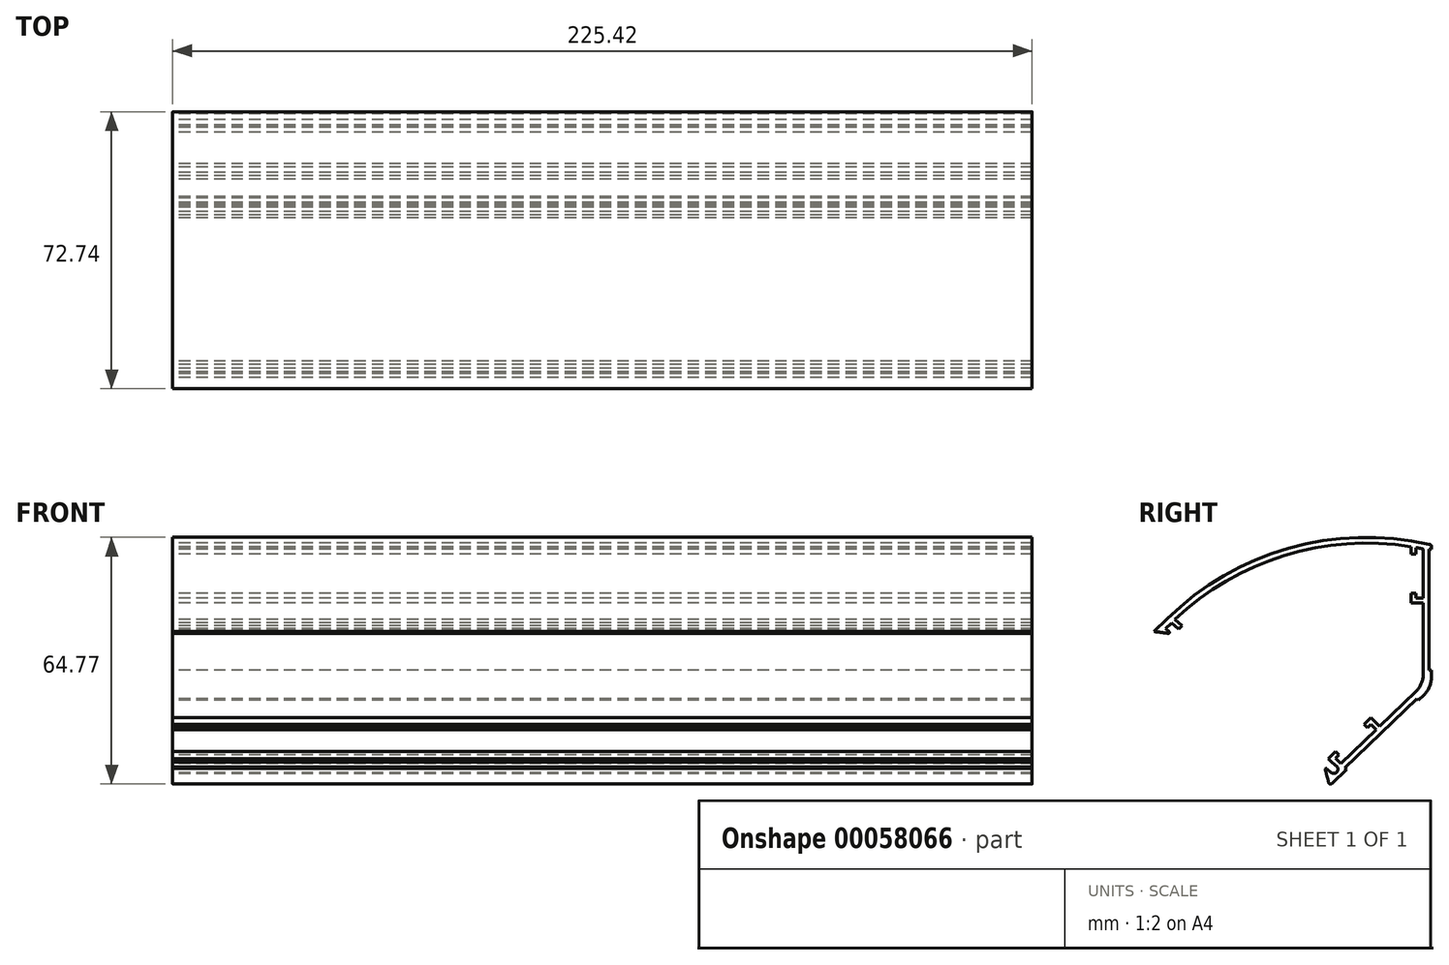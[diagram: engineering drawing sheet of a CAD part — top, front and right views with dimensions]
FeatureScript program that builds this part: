
annotation { "Feature Type Name" : "Feature", "Feature Type Description" : "" }
export const myFeature = defineFeature(function(context is Context, id is Id, definition is map)
    precondition{}
    {
        {
            var Q0;
            Q0=qCreatedBy(makeId("Right.planeOp"),FACE);
            var sketch = newSketch(context, id + "F0", { "sketchPlane" : qUnion([Q0])});
            skLineSegment(sketch, "E0", {"start": v(-26.31, -25.4) * mm, "end": v(0, 0) * mm});
            skLineSegment(sketch, "E1", {"start": v(0, 0) * mm, "end": v(0, 37.34) * mm});
            skArc(sketch, "E2", {"start": v(0, 37.34) * mm, "mid": v(-36.86, 36.32) * mm, "end": v(-68.74, 17.77) * mm});
            skLineSegment(sketch, "E3", {"start": v(-68.74, 17.77) * mm, "end": v(-72.14, 14.43) * mm});
            skLineSegment(sketch, "E4", {"start": v(-26.31, -25.4) * mm, "end": v(-72.14, 14.43) * mm});
            skLineSegment(sketch, "E5", {"start": v(-68.74, 17.77) * mm, "end": v(-26.31, -25.4) * mm, "construction": true});
            skSolve(sketch);
        }
        {
            var Q0;
            Q0=qSketchRegion(id+"F0",true);
            extrude(context, id + "F1", {"entities" : qUnion([Q0]), "endBound" : BoundingType.SYMMETRIC, "depth" : 225.42 * mm});
        }
        {
            var Q0;
            Q0=makeQuery(id+"F1.opExtrude","SWEPT_FACE",FACE,{"disambiguationData":[OSD([sQuery(id+"F0.wireOp",EDGE,"E4")])]});
            var Q1;
            Q1=makeQuery(id+"F1.opExtrude","CAP_FACE",FACE,{"disambiguationData":[OSD([sQuery(id+"F0.wireOp",EDGE,"E0"),sQuery(id+"F0.wireOp",EDGE,"E1"),sQuery(id+"F0.wireOp",EDGE,"E2"),sQuery(id+"F0.wireOp",EDGE,"E3"),sQuery(id+"F0.wireOp",EDGE,"E4")])],"isStart":true});
            var Q2;
            Q2=makeQuery(id+"F1.opExtrude","CAP_FACE",FACE,{"disambiguationData":[OSD([sQuery(id+"F0.wireOp",EDGE,"E0"),sQuery(id+"F0.wireOp",EDGE,"E1"),sQuery(id+"F0.wireOp",EDGE,"E2"),sQuery(id+"F0.wireOp",EDGE,"E3"),sQuery(id+"F0.wireOp",EDGE,"E4")])],"isStart":false});
            shell(context, id + "F2", {"entities" : qUnion([Q0, Q1, Q2]), "thickness" : 1.52 * mm});
        }
        {
            var Q0;
            Q0=makeQuery(id+"F1.opExtrude","CAP_FACE",FACE,{"disambiguationData":[OSD([sQuery(id+"F0.wireOp",EDGE,"E0"),sQuery(id+"F0.wireOp",EDGE,"E1"),sQuery(id+"F0.wireOp",EDGE,"E2"),sQuery(id+"F0.wireOp",EDGE,"E3"),sQuery(id+"F0.wireOp",EDGE,"E4")])],"isStart":true});
            var sketch = newSketch(context, id + "F3", { "sketchPlane" : qUnion([Q0])});
            skLineSegment(sketch, "E6", {"start": v(72.14, 14.43) * mm, "end": v(26.31, -25.4) * mm, "construction": true});
            skSolve(sketch);
        }
        {
            var Q0;
            {var subQ6=sQuery(id+"F0.wireOp",EDGE,"E0");var subQ7=makeQuery(id+"F1.opExtrude","CAP_EDGE",EDGE,{"disambiguationData":[OSD([subQ6])],"isStart":true});Q0=makeQuery(id+"F3.imprint","IMPRINT",FACE,{"disambiguationData":[TD([[makeQuery(id+"F3.imprint","IMPRINT",EDGE,{"derivedFrom":subQ7}),-1.0]])]});}
            var sketch = newSketch(context, id + "F4", { "sketchPlane" : qUnion([Q0])});
            skLineSegment(sketch, "E7", {"start": v(70.98, 13.42) * mm, "end": v(69.17, 15.2) * mm});
            skLineSegment(sketch, "E8", {"start": v(69.17, 15.2) * mm, "end": v(67.25, 13.54) * mm});
            skLineSegment(sketch, "E9", {"start": v(67.25, 13.54) * mm, "end": v(69.07, 11.76) * mm});
            skLineSegment(sketch, "E10", {"start": v(69.07, 11.76) * mm, "end": v(70.98, 13.42) * mm});
            skSolve(sketch);
        }
        {
            var Q0;
            Q0=qSketchRegion(id+"F4",true);
            var Q1;
            Q1=makeQuery(id+"F1.opExtrude","CAP_FACE",FACE,{"disambiguationData":[OSD([sQuery(id+"F0.wireOp",EDGE,"E0"),sQuery(id+"F0.wireOp",EDGE,"E1"),sQuery(id+"F0.wireOp",EDGE,"E2"),sQuery(id+"F0.wireOp",EDGE,"E3"),sQuery(id+"F0.wireOp",EDGE,"E4")])],"isStart":false});
            extrude(context, id + "F5", {"entities" : qUnion([Q0]), "operationType" : NewBodyOperationType.ADD, "endBound" : BoundingType.UP_TO_SURFACE, "oppositeDirection" : true, "endBoundEntityFace" : qUnion([Q1]), "depth" : 25.4 * mm});
        }
        {
            var Q0;
            {var subQ6=sQuery(id+"F0.wireOp",EDGE,"E0");var subQ7=makeQuery(id+"F1.opExtrude","CAP_EDGE",EDGE,{"disambiguationData":[OSD([subQ6])],"isStart":true});Q0=makeQuery(id+"F3.imprint","IMPRINT",FACE,{"disambiguationData":[TD([[makeQuery(id+"F3.imprint","IMPRINT",EDGE,{"derivedFrom":subQ7}),-1.0]])]});}
            var sketch = newSketch(context, id + "F6", { "sketchPlane" : qUnion([Q0])});
            skLineSegment(sketch, "E11", {"start": v(25.64, -22.64) * mm, "end": v(27.47, -24.4) * mm});
            skLineSegment(sketch, "E12", {"start": v(27.47, -24.4) * mm, "end": v(29.38, -22.74) * mm});
            skLineSegment(sketch, "E13", {"start": v(29.38, -22.74) * mm, "end": v(27.55, -20.97) * mm});
            skLineSegment(sketch, "E14", {"start": v(27.55, -20.97) * mm, "end": v(25.64, -22.64) * mm});
            skSolve(sketch);
        }
        {
            var Q0;
            Q0=qSketchRegion(id+"F6",true);
            var Q1;
            Q1=makeQuery(id+"F5.boolean.opBoolean","MERGE",FACE,{"derivedFrom":[makeQuery(id+"F1.opExtrude","CAP_FACE",FACE,{"disambiguationData":[OSD([sQuery(id+"F0.wireOp",EDGE,"E0"),sQuery(id+"F0.wireOp",EDGE,"E1"),sQuery(id+"F0.wireOp",EDGE,"E2"),sQuery(id+"F0.wireOp",EDGE,"E3"),sQuery(id+"F0.wireOp",EDGE,"E4")])],"isStart":false}),makeQuery(id+"F5.opExtrude","CAP_FACE",FACE,{"disambiguationData":[OSD([sQuery(id+"F4.wireOp",EDGE,"E7"),sQuery(id+"F4.wireOp",EDGE,"E8"),sQuery(id+"F4.wireOp",EDGE,"E9"),sQuery(id+"F4.wireOp",EDGE,"E10")])],"isStart":false})]});
            extrude(context, id + "F7", {"entities" : qUnion([Q0]), "operationType" : NewBodyOperationType.ADD, "endBound" : BoundingType.UP_TO_SURFACE, "oppositeDirection" : true, "endBoundEntityFace" : qUnion([Q1]), "depth" : 25.4 * mm});
        }
        {
            var Q0;
            {var subQ6=sQuery(id+"F0.wireOp",EDGE,"E0");var subQ7=makeQuery(id+"F1.opExtrude","CAP_EDGE",EDGE,{"disambiguationData":[OSD([subQ6])],"isStart":true});Q0=makeQuery(id+"F3.imprint","IMPRINT",FACE,{"disambiguationData":[TD([[makeQuery(id+"F3.imprint","IMPRINT",EDGE,{"derivedFrom":subQ7}),-1.0]])]});}
            var sketch = newSketch(context, id + "F8", { "sketchPlane" : qUnion([Q0])});
            skCircle(sketch, "E15", {"center": v(76.77, -37.18) * mm, "radius": 51.8 * mm});
            skSolve(sketch);
        }
        {
            var Q0;
            Q0=qSketchRegion(id+"F8",true);
            var Q1;
            Q1=makeQuery(id+"F7.boolean.opBoolean","MERGE",FACE,{"derivedFrom":[makeQuery(id+"F5.boolean.opBoolean","MERGE",FACE,{"derivedFrom":[makeQuery(id+"F1.opExtrude","CAP_FACE",FACE,{"disambiguationData":[OSD([sQuery(id+"F0.wireOp",EDGE,"E0"),sQuery(id+"F0.wireOp",EDGE,"E1"),sQuery(id+"F0.wireOp",EDGE,"E2"),sQuery(id+"F0.wireOp",EDGE,"E3"),sQuery(id+"F0.wireOp",EDGE,"E4")])],"isStart":false}),makeQuery(id+"F5.opExtrude","CAP_FACE",FACE,{"disambiguationData":[OSD([sQuery(id+"F4.wireOp",EDGE,"E7"),sQuery(id+"F4.wireOp",EDGE,"E8"),sQuery(id+"F4.wireOp",EDGE,"E9"),sQuery(id+"F4.wireOp",EDGE,"E10")])],"isStart":false})]}),makeQuery(id+"F7.opExtrude","CAP_FACE",FACE,{"disambiguationData":[OSD([sQuery(id+"F6.wireOp",EDGE,"E11"),sQuery(id+"F6.wireOp",EDGE,"E12"),sQuery(id+"F6.wireOp",EDGE,"E13"),sQuery(id+"F6.wireOp",EDGE,"E14")])],"isStart":false})]});
            extrude(context, id + "F9", {"entities" : qUnion([Q0]), "operationType" : NewBodyOperationType.REMOVE, "endBound" : BoundingType.UP_TO_SURFACE, "oppositeDirection" : true, "endBoundEntityFace" : qUnion([Q1]), "depth" : 25.4 * mm});
        }
        {
            var Q0;
            {var subQ6=sQuery(id+"F0.wireOp",EDGE,"E0");var subQ7=makeQuery(id+"F1.opExtrude","CAP_EDGE",EDGE,{"disambiguationData":[OSD([subQ6])],"isStart":true});Q0=makeQuery(id+"F3.imprint","IMPRINT",FACE,{"disambiguationData":[TD([[makeQuery(id+"F3.imprint","IMPRINT",EDGE,{"derivedFrom":subQ7}),-1.0]])]});}
            var sketch = newSketch(context, id + "F10", { "sketchPlane" : qUnion([Q0])});
            skLineSegment(sketch, "E16", {"start": v(24.08, -21.14) * mm, "end": v(25.57, -19.85) * mm});
            skLineSegment(sketch, "E17", {"start": v(25.57, -19.85) * mm, "end": v(24.53, -18.85) * mm});
            skLineSegment(sketch, "E18", {"start": v(24.53, -18.85) * mm, "end": v(23.17, -20.26) * mm});
            skLineSegment(sketch, "E19", {"start": v(23.17, -20.26) * mm, "end": v(24.08, -21.14) * mm});
            skSolve(sketch);
        }
        {
            var Q0;
            {var subQ6=sQuery(id+"F0.wireOp",EDGE,"E0");var subQ7=makeQuery(id+"F1.opExtrude","CAP_EDGE",EDGE,{"disambiguationData":[OSD([subQ6])],"isStart":true});Q0=makeQuery(id+"F3.imprint","IMPRINT",FACE,{"disambiguationData":[TD([[makeQuery(id+"F3.imprint","IMPRINT",EDGE,{"derivedFrom":subQ7}),-1.0]])]});}
            var sketch = newSketch(context, id + "F11", { "sketchPlane" : qUnion([Q0])});
            skLineSegment(sketch, "E20", {"start": v(25.57, -19.85) * mm, "end": v(23.62, -17.97) * mm});
            skLineSegment(sketch, "E21", {"start": v(23.62, -17.97) * mm, "end": v(24.5, -17.06) * mm});
            skLineSegment(sketch, "E22", {"start": v(24.5, -17.06) * mm, "end": v(26.45, -18.94) * mm});
            skLineSegment(sketch, "E23", {"start": v(26.45, -18.94) * mm, "end": v(25.57, -19.85) * mm});
            skSolve(sketch);
        }
        {
            var Q0;
            {var subQ6=sQuery(id+"F0.wireOp",EDGE,"E0");var subQ7=makeQuery(id+"F1.opExtrude","CAP_EDGE",EDGE,{"disambiguationData":[OSD([subQ6])],"isStart":true});Q0=makeQuery(id+"F3.imprint","IMPRINT",FACE,{"disambiguationData":[TD([[makeQuery(id+"F3.imprint","IMPRINT",EDGE,{"derivedFrom":subQ7}),-1.0]])]});}
            var sketch = newSketch(context, id + "F12", { "sketchPlane" : qUnion([Q0])});
            skLineSegment(sketch, "E24", {"start": v(67.63, 16.72) * mm, "end": v(65.71, 15.05) * mm});
            skLineSegment(sketch, "E25", {"start": v(65.71, 15.05) * mm, "end": v(64.8, 15.94) * mm});
            skLineSegment(sketch, "E26", {"start": v(64.8, 15.94) * mm, "end": v(66.72, 17.6) * mm});
            skLineSegment(sketch, "E27", {"start": v(66.72, 17.6) * mm, "end": v(67.63, 16.72) * mm});
            skSolve(sketch);
        }
        {
            var Q0;
            {var subQ6=sQuery(id+"F0.wireOp",EDGE,"E0");var subQ7=makeQuery(id+"F1.opExtrude","CAP_EDGE",EDGE,{"disambiguationData":[OSD([subQ6])],"isStart":true});Q0=makeQuery(id+"F3.imprint","IMPRINT",FACE,{"disambiguationData":[TD([[makeQuery(id+"F3.imprint","IMPRINT",EDGE,{"derivedFrom":subQ7}),-1.0]])]});}
            var sketch = newSketch(context, id + "F13", { "sketchPlane" : qUnion([Q0])});
            skLineSegment(sketch, "E28", {"start": v(13.94, -11.35) * mm, "end": v(15.3, -9.94) * mm});
            skLineSegment(sketch, "E29", {"start": v(15.3, -9.94) * mm, "end": v(16.22, -10.82) * mm});
            skLineSegment(sketch, "E30", {"start": v(16.22, -10.82) * mm, "end": v(17.1, -9.9) * mm});
            skLineSegment(sketch, "E31", {"start": v(17.1, -9.9) * mm, "end": v(15.27, -8.14) * mm});
            skLineSegment(sketch, "E32", {"start": v(15.27, -8.14) * mm, "end": v(13.03, -10.47) * mm});
            skLineSegment(sketch, "E33", {"start": v(13.03, -10.47) * mm, "end": v(13.94, -11.35) * mm});
            skSolve(sketch);
        }
        {
            var Q0;
            {var subQ6=sQuery(id+"F12.wireOp",EDGE,"E27");Q0=makeQuery(id+"F12.imprint","IMPRINT",FACE,{"disambiguationData":[TD([[makeQuery(id+"F12.imprint","IMPRINT",EDGE,{"derivedFrom":subQ6}),1.0]])]});}
            var sketch = newSketch(context, id + "F14", { "sketchPlane" : qUnion([Q0])});
            skLineSegment(sketch, "E34", {"start": v(1.52, 22.01) * mm, "end": v(1.52, 23.28) * mm});
            skLineSegment(sketch, "E35", {"start": v(1.52, 23.28) * mm, "end": v(3.48, 23.28) * mm});
            skLineSegment(sketch, "E36", {"start": v(3.48, 23.28) * mm, "end": v(3.48, 24.55) * mm});
            skLineSegment(sketch, "E37", {"start": v(3.48, 24.55) * mm, "end": v(4.75, 24.55) * mm});
            skLineSegment(sketch, "E38", {"start": v(4.75, 24.55) * mm, "end": v(4.75, 22.01) * mm});
            skLineSegment(sketch, "E39", {"start": v(4.75, 22.01) * mm, "end": v(1.52, 22.01) * mm});
            skLineSegment(sketch, "E40", {"start": v(3.48, 36.7) * mm, "end": v(3.48, 34.84) * mm});
            skLineSegment(sketch, "E41", {"start": v(3.48, 34.84) * mm, "end": v(4.75, 34.84) * mm});
            skLineSegment(sketch, "E42", {"start": v(4.75, 34.84) * mm, "end": v(4.75, 36.7) * mm});
            skLineSegment(sketch, "E43", {"start": v(4.75, 36.7) * mm, "end": v(3.48, 36.7) * mm});
            skSolve(sketch);
        }
        {
            var Q0;
            Q0=qSketchRegion(id+"F10",true);
            var Q1;
            Q1=qSketchRegion(id+"F11",true);
            var Q2;
            Q2=qSketchRegion(id+"F12",true);
            var Q3;
            Q3=qSketchRegion(id+"F13",true);
            var Q4;
            Q4=qSketchRegion(id+"F14",true);
            var Q5;
            Q5=makeQuery(id+"F7.boolean.opBoolean","MERGE",FACE,{"derivedFrom":[makeQuery(id+"F5.boolean.opBoolean","MERGE",FACE,{"derivedFrom":[makeQuery(id+"F1.opExtrude","CAP_FACE",FACE,{"disambiguationData":[OSD([sQuery(id+"F0.wireOp",EDGE,"E0"),sQuery(id+"F0.wireOp",EDGE,"E1"),sQuery(id+"F0.wireOp",EDGE,"E2"),sQuery(id+"F0.wireOp",EDGE,"E3"),sQuery(id+"F0.wireOp",EDGE,"E4")])],"isStart":false}),makeQuery(id+"F5.opExtrude","CAP_FACE",FACE,{"disambiguationData":[OSD([sQuery(id+"F4.wireOp",EDGE,"E7"),sQuery(id+"F4.wireOp",EDGE,"E8"),sQuery(id+"F4.wireOp",EDGE,"E9"),sQuery(id+"F4.wireOp",EDGE,"E10")])],"isStart":false})]}),makeQuery(id+"F7.opExtrude","CAP_FACE",FACE,{"disambiguationData":[OSD([sQuery(id+"F6.wireOp",EDGE,"E11"),sQuery(id+"F6.wireOp",EDGE,"E12"),sQuery(id+"F6.wireOp",EDGE,"E13"),sQuery(id+"F6.wireOp",EDGE,"E14")])],"isStart":false})]});
            extrude(context, id + "F15", {"entities" : qUnion([Q0, Q1, Q2, Q3, Q4]), "operationType" : NewBodyOperationType.ADD, "endBound" : BoundingType.UP_TO_SURFACE, "oppositeDirection" : true, "endBoundEntityFace" : qUnion([Q5]), "depth" : 25.4 * mm});
        }
        {
            var Q0;
            Q0=makeQuery(id+"F15.boolean.opBoolean","MERGE",FACE,{"derivedFrom":[makeQuery(id+"F7.boolean.opBoolean","MERGE",FACE,{"derivedFrom":[makeQuery(id+"F5.boolean.opBoolean","MERGE",FACE,{"derivedFrom":[makeQuery(id+"F1.opExtrude","CAP_FACE",FACE,{"disambiguationData":[OSD([sQuery(id+"F0.wireOp",EDGE,"E0"),sQuery(id+"F0.wireOp",EDGE,"E1"),sQuery(id+"F0.wireOp",EDGE,"E2"),sQuery(id+"F0.wireOp",EDGE,"E3"),sQuery(id+"F0.wireOp",EDGE,"E4")])],"isStart":true}),makeQuery(id+"F5.opExtrude","CAP_FACE",FACE,{"disambiguationData":[OSD([sQuery(id+"F4.wireOp",EDGE,"E7"),sQuery(id+"F4.wireOp",EDGE,"E8"),sQuery(id+"F4.wireOp",EDGE,"E9"),sQuery(id+"F4.wireOp",EDGE,"E10")])],"isStart":true})]}),makeQuery(id+"F7.opExtrude","CAP_FACE",FACE,{"disambiguationData":[OSD([sQuery(id+"F6.wireOp",EDGE,"E11"),sQuery(id+"F6.wireOp",EDGE,"E12"),sQuery(id+"F6.wireOp",EDGE,"E13"),sQuery(id+"F6.wireOp",EDGE,"E14")])],"isStart":true})]}),makeQuery(id+"F15.opExtrude","CAP_FACE",FACE,{"disambiguationData":[OSD([sQuery(id+"F10.wireOp",EDGE,"E16"),sQuery(id+"F10.wireOp",EDGE,"E17"),sQuery(id+"F10.wireOp",EDGE,"E18"),sQuery(id+"F10.wireOp",EDGE,"E19")])],"isStart":true}),makeQuery(id+"F15.opExtrude","CAP_FACE",FACE,{"disambiguationData":[OSD([sQuery(id+"F11.wireOp",EDGE,"E20"),sQuery(id+"F11.wireOp",EDGE,"E21"),sQuery(id+"F11.wireOp",EDGE,"E22"),sQuery(id+"F11.wireOp",EDGE,"E23")])],"isStart":true}),makeQuery(id+"F15.opExtrude","CAP_FACE",FACE,{"disambiguationData":[OSD([sQuery(id+"F12.wireOp",EDGE,"E24"),sQuery(id+"F12.wireOp",EDGE,"E25"),sQuery(id+"F12.wireOp",EDGE,"E26"),sQuery(id+"F12.wireOp",EDGE,"E27")])],"isStart":true}),makeQuery(id+"F15.opExtrude","CAP_FACE",FACE,{"disambiguationData":[OSD([sQuery(id+"F13.wireOp",EDGE,"E28"),sQuery(id+"F13.wireOp",EDGE,"E29"),sQuery(id+"F13.wireOp",EDGE,"E30"),sQuery(id+"F13.wireOp",EDGE,"E31"),sQuery(id+"F13.wireOp",EDGE,"E32"),sQuery(id+"F13.wireOp",EDGE,"E33")])],"isStart":true}),makeQuery(id+"F15.opExtrude","CAP_FACE",FACE,{"disambiguationData":[OSD([sQuery(id+"F14.wireOp",EDGE,"E34"),sQuery(id+"F14.wireOp",EDGE,"E35"),sQuery(id+"F14.wireOp",EDGE,"E36"),sQuery(id+"F14.wireOp",EDGE,"E37"),sQuery(id+"F14.wireOp",EDGE,"E38"),sQuery(id+"F14.wireOp",EDGE,"E39")])],"isStart":true}),makeQuery(id+"F15.opExtrude","CAP_FACE",FACE,{"disambiguationData":[OSD([sQuery(id+"F14.wireOp",EDGE,"E40"),sQuery(id+"F14.wireOp",EDGE,"E41"),sQuery(id+"F14.wireOp",EDGE,"E42"),sQuery(id+"F14.wireOp",EDGE,"E43")])],"isStart":true})]});
            var sketch = newSketch(context, id + "F16", { "sketchPlane" : qUnion([Q0])});
            skLineSegment(sketch, "E44.0", {"start": v(-0.6, -0.25) * mm, "end": v(-0.6, 37.2) * mm});
            skLineSegment(sketch, "E44.1", {"start": v(26.15, -26.08) * mm, "end": v(-0.6, -0.25) * mm});
            skLineSegment(sketch, "E45", {"start": v(-0.6, 37.2) * mm, "end": v(0, 37.34) * mm});
            skLineSegment(sketch, "E46", {"start": v(26.31, -25.4) * mm, "end": v(26.15, -26.08) * mm});
            skLineSegment(sketch, "E47", {"start": v(26.31, -25.4) * mm, "end": v(0, 0) * mm});
            skLineSegment(sketch, "E48", {"start": v(0, 0) * mm, "end": v(0, 37.34) * mm});
            skSolve(sketch);
        }
        {
            var Q0;
            Q0 = qSketchRegion(id + "F16", true);
            var Q1;
            Q1=makeQuery(id+"F15.boolean.opBoolean","MERGE",FACE,{"derivedFrom":[makeQuery(id+"F7.boolean.opBoolean","MERGE",FACE,{"derivedFrom":[makeQuery(id+"F5.boolean.opBoolean","MERGE",FACE,{"derivedFrom":[makeQuery(id+"F1.opExtrude","CAP_FACE",FACE,{"disambiguationData":[OSD([sQuery(id+"F0.wireOp",EDGE,"E0"),sQuery(id+"F0.wireOp",EDGE,"E1"),sQuery(id+"F0.wireOp",EDGE,"E2"),sQuery(id+"F0.wireOp",EDGE,"E3"),sQuery(id+"F0.wireOp",EDGE,"E4")])],"isStart":false}),makeQuery(id+"F5.opExtrude","CAP_FACE",FACE,{"disambiguationData":[OSD([sQuery(id+"F4.wireOp",EDGE,"E7"),sQuery(id+"F4.wireOp",EDGE,"E8"),sQuery(id+"F4.wireOp",EDGE,"E9"),sQuery(id+"F4.wireOp",EDGE,"E10")])],"isStart":false})]}),makeQuery(id+"F7.opExtrude","CAP_FACE",FACE,{"disambiguationData":[OSD([sQuery(id+"F6.wireOp",EDGE,"E11"),sQuery(id+"F6.wireOp",EDGE,"E12"),sQuery(id+"F6.wireOp",EDGE,"E13"),sQuery(id+"F6.wireOp",EDGE,"E14")])],"isStart":false})]}),makeQuery(id+"F15.opExtrude","CAP_FACE",FACE,{"disambiguationData":[OSD([sQuery(id+"F10.wireOp",EDGE,"E16"),sQuery(id+"F10.wireOp",EDGE,"E17"),sQuery(id+"F10.wireOp",EDGE,"E18"),sQuery(id+"F10.wireOp",EDGE,"E19")])],"isStart":false}),makeQuery(id+"F15.opExtrude","CAP_FACE",FACE,{"disambiguationData":[OSD([sQuery(id+"F11.wireOp",EDGE,"E20"),sQuery(id+"F11.wireOp",EDGE,"E21"),sQuery(id+"F11.wireOp",EDGE,"E22"),sQuery(id+"F11.wireOp",EDGE,"E23")])],"isStart":false}),makeQuery(id+"F15.opExtrude","CAP_FACE",FACE,{"disambiguationData":[OSD([sQuery(id+"F12.wireOp",EDGE,"E24"),sQuery(id+"F12.wireOp",EDGE,"E25"),sQuery(id+"F12.wireOp",EDGE,"E26"),sQuery(id+"F12.wireOp",EDGE,"E27")])],"isStart":false}),makeQuery(id+"F15.opExtrude","CAP_FACE",FACE,{"disambiguationData":[OSD([sQuery(id+"F13.wireOp",EDGE,"E28"),sQuery(id+"F13.wireOp",EDGE,"E29"),sQuery(id+"F13.wireOp",EDGE,"E30"),sQuery(id+"F13.wireOp",EDGE,"E31"),sQuery(id+"F13.wireOp",EDGE,"E32"),sQuery(id+"F13.wireOp",EDGE,"E33")])],"isStart":false}),makeQuery(id+"F15.opExtrude","CAP_FACE",FACE,{"disambiguationData":[OSD([sQuery(id+"F14.wireOp",EDGE,"E34"),sQuery(id+"F14.wireOp",EDGE,"E35"),sQuery(id+"F14.wireOp",EDGE,"E36"),sQuery(id+"F14.wireOp",EDGE,"E37"),sQuery(id+"F14.wireOp",EDGE,"E38"),sQuery(id+"F14.wireOp",EDGE,"E39")])],"isStart":false}),makeQuery(id+"F15.opExtrude","CAP_FACE",FACE,{"disambiguationData":[OSD([sQuery(id+"F14.wireOp",EDGE,"E40"),sQuery(id+"F14.wireOp",EDGE,"E41"),sQuery(id+"F14.wireOp",EDGE,"E42"),sQuery(id+"F14.wireOp",EDGE,"E43")])],"isStart":false})]});
            extrude(context, id + "F17", {"entities" : qUnion([Q0]), "operationType" : NewBodyOperationType.ADD, "endBound" : BoundingType.UP_TO_SURFACE, "oppositeDirection" : true, "endBoundEntityFace" : qUnion([Q1]), "depth" : 25.4 * mm});
        }
        {
            var Q0;
            Q0=makeQuery(id+"F17.boolean.opBoolean","MERGE",FACE,{"derivedFrom":[makeQuery(id+"F15.boolean.opBoolean","MERGE",FACE,{"derivedFrom":[makeQuery(id+"F7.boolean.opBoolean","MERGE",FACE,{"derivedFrom":[makeQuery(id+"F5.boolean.opBoolean","MERGE",FACE,{"derivedFrom":[makeQuery(id+"F1.opExtrude","CAP_FACE",FACE,{"disambiguationData":[OSD([sQuery(id+"F0.wireOp",EDGE,"E0"),sQuery(id+"F0.wireOp",EDGE,"E1"),sQuery(id+"F0.wireOp",EDGE,"E2"),sQuery(id+"F0.wireOp",EDGE,"E3"),sQuery(id+"F0.wireOp",EDGE,"E4")])],"isStart":true}),makeQuery(id+"F5.opExtrude","CAP_FACE",FACE,{"disambiguationData":[OSD([sQuery(id+"F4.wireOp",EDGE,"E7"),sQuery(id+"F4.wireOp",EDGE,"E8"),sQuery(id+"F4.wireOp",EDGE,"E9"),sQuery(id+"F4.wireOp",EDGE,"E10")])],"isStart":true})]}),makeQuery(id+"F7.opExtrude","CAP_FACE",FACE,{"disambiguationData":[OSD([sQuery(id+"F6.wireOp",EDGE,"E11"),sQuery(id+"F6.wireOp",EDGE,"E12"),sQuery(id+"F6.wireOp",EDGE,"E13"),sQuery(id+"F6.wireOp",EDGE,"E14")])],"isStart":true})]}),makeQuery(id+"F15.opExtrude","CAP_FACE",FACE,{"disambiguationData":[OSD([sQuery(id+"F10.wireOp",EDGE,"E16"),sQuery(id+"F10.wireOp",EDGE,"E17"),sQuery(id+"F10.wireOp",EDGE,"E18"),sQuery(id+"F10.wireOp",EDGE,"E19")])],"isStart":true}),makeQuery(id+"F15.opExtrude","CAP_FACE",FACE,{"disambiguationData":[OSD([sQuery(id+"F11.wireOp",EDGE,"E20"),sQuery(id+"F11.wireOp",EDGE,"E21"),sQuery(id+"F11.wireOp",EDGE,"E22"),sQuery(id+"F11.wireOp",EDGE,"E23")])],"isStart":true}),makeQuery(id+"F15.opExtrude","CAP_FACE",FACE,{"disambiguationData":[OSD([sQuery(id+"F12.wireOp",EDGE,"E24"),sQuery(id+"F12.wireOp",EDGE,"E25"),sQuery(id+"F12.wireOp",EDGE,"E26"),sQuery(id+"F12.wireOp",EDGE,"E27")])],"isStart":true}),makeQuery(id+"F15.opExtrude","CAP_FACE",FACE,{"disambiguationData":[OSD([sQuery(id+"F13.wireOp",EDGE,"E28"),sQuery(id+"F13.wireOp",EDGE,"E29"),sQuery(id+"F13.wireOp",EDGE,"E30"),sQuery(id+"F13.wireOp",EDGE,"E31"),sQuery(id+"F13.wireOp",EDGE,"E32"),sQuery(id+"F13.wireOp",EDGE,"E33")])],"isStart":true}),makeQuery(id+"F15.opExtrude","CAP_FACE",FACE,{"disambiguationData":[OSD([sQuery(id+"F14.wireOp",EDGE,"E34"),sQuery(id+"F14.wireOp",EDGE,"E35"),sQuery(id+"F14.wireOp",EDGE,"E36"),sQuery(id+"F14.wireOp",EDGE,"E37"),sQuery(id+"F14.wireOp",EDGE,"E38"),sQuery(id+"F14.wireOp",EDGE,"E39")])],"isStart":true}),makeQuery(id+"F15.opExtrude","CAP_FACE",FACE,{"disambiguationData":[OSD([sQuery(id+"F14.wireOp",EDGE,"E40"),sQuery(id+"F14.wireOp",EDGE,"E41"),sQuery(id+"F14.wireOp",EDGE,"E42"),sQuery(id+"F14.wireOp",EDGE,"E43")])],"isStart":true})]}),makeQuery(id+"F17.opExtrude","CAP_FACE",FACE,{"disambiguationData":[OSD([sQuery(id+"F16.wireOp",EDGE,"E44.0"),sQuery(id+"F16.wireOp",EDGE,"E44.1"),sQuery(id+"F16.wireOp",EDGE,"E45"),sQuery(id+"F16.wireOp",EDGE,"E46"),sQuery(id+"F16.wireOp",EDGE,"E47"),sQuery(id+"F16.wireOp",EDGE,"E48")])],"isStart":true})]});
            var sketch = newSketch(context, id + "F18", { "sketchPlane" : qUnion([Q0])});
            skLineSegment(sketch, "E49.bottom", {"start": v(-0.6, 36.1) * mm, "end": v(0, 36.1) * mm});
            skLineSegment(sketch, "E49.top", {"start": v(-0.6, 4.36) * mm, "end": v(0, 4.36) * mm});
            skLineSegment(sketch, "E49.left", {"start": v(-0.6, 36.1) * mm, "end": v(-0.6, 4.36) * mm});
            skLineSegment(sketch, "E49.right", {"start": v(0, 36.1) * mm, "end": v(0, 4.36) * mm});
            skSolve(sketch);
        }
        {
            var Q0;
            Q0 = qSketchRegion(id + "F18", true);
            var Q1;
            Q1=makeQuery(id+"F17.boolean.opBoolean","MERGE",FACE,{"derivedFrom":[makeQuery(id+"F15.boolean.opBoolean","MERGE",FACE,{"derivedFrom":[makeQuery(id+"F7.boolean.opBoolean","MERGE",FACE,{"derivedFrom":[makeQuery(id+"F5.boolean.opBoolean","MERGE",FACE,{"derivedFrom":[makeQuery(id+"F1.opExtrude","CAP_FACE",FACE,{"disambiguationData":[OSD([sQuery(id+"F0.wireOp",EDGE,"E0"),sQuery(id+"F0.wireOp",EDGE,"E1"),sQuery(id+"F0.wireOp",EDGE,"E2"),sQuery(id+"F0.wireOp",EDGE,"E3"),sQuery(id+"F0.wireOp",EDGE,"E4")])],"isStart":false}),makeQuery(id+"F5.opExtrude","CAP_FACE",FACE,{"disambiguationData":[OSD([sQuery(id+"F4.wireOp",EDGE,"E7"),sQuery(id+"F4.wireOp",EDGE,"E8"),sQuery(id+"F4.wireOp",EDGE,"E9"),sQuery(id+"F4.wireOp",EDGE,"E10")])],"isStart":false})]}),makeQuery(id+"F7.opExtrude","CAP_FACE",FACE,{"disambiguationData":[OSD([sQuery(id+"F6.wireOp",EDGE,"E11"),sQuery(id+"F6.wireOp",EDGE,"E12"),sQuery(id+"F6.wireOp",EDGE,"E13"),sQuery(id+"F6.wireOp",EDGE,"E14")])],"isStart":false})]}),makeQuery(id+"F15.opExtrude","CAP_FACE",FACE,{"disambiguationData":[OSD([sQuery(id+"F10.wireOp",EDGE,"E16"),sQuery(id+"F10.wireOp",EDGE,"E17"),sQuery(id+"F10.wireOp",EDGE,"E18"),sQuery(id+"F10.wireOp",EDGE,"E19")])],"isStart":false}),makeQuery(id+"F15.opExtrude","CAP_FACE",FACE,{"disambiguationData":[OSD([sQuery(id+"F11.wireOp",EDGE,"E20"),sQuery(id+"F11.wireOp",EDGE,"E21"),sQuery(id+"F11.wireOp",EDGE,"E22"),sQuery(id+"F11.wireOp",EDGE,"E23")])],"isStart":false}),makeQuery(id+"F15.opExtrude","CAP_FACE",FACE,{"disambiguationData":[OSD([sQuery(id+"F12.wireOp",EDGE,"E24"),sQuery(id+"F12.wireOp",EDGE,"E25"),sQuery(id+"F12.wireOp",EDGE,"E26"),sQuery(id+"F12.wireOp",EDGE,"E27")])],"isStart":false}),makeQuery(id+"F15.opExtrude","CAP_FACE",FACE,{"disambiguationData":[OSD([sQuery(id+"F13.wireOp",EDGE,"E28"),sQuery(id+"F13.wireOp",EDGE,"E29"),sQuery(id+"F13.wireOp",EDGE,"E30"),sQuery(id+"F13.wireOp",EDGE,"E31"),sQuery(id+"F13.wireOp",EDGE,"E32"),sQuery(id+"F13.wireOp",EDGE,"E33")])],"isStart":false}),makeQuery(id+"F15.opExtrude","CAP_FACE",FACE,{"disambiguationData":[OSD([sQuery(id+"F14.wireOp",EDGE,"E34"),sQuery(id+"F14.wireOp",EDGE,"E35"),sQuery(id+"F14.wireOp",EDGE,"E36"),sQuery(id+"F14.wireOp",EDGE,"E37"),sQuery(id+"F14.wireOp",EDGE,"E38"),sQuery(id+"F14.wireOp",EDGE,"E39")])],"isStart":false}),makeQuery(id+"F15.opExtrude","CAP_FACE",FACE,{"disambiguationData":[OSD([sQuery(id+"F14.wireOp",EDGE,"E40"),sQuery(id+"F14.wireOp",EDGE,"E41"),sQuery(id+"F14.wireOp",EDGE,"E42"),sQuery(id+"F14.wireOp",EDGE,"E43")])],"isStart":false})]}),makeQuery(id+"F17.opExtrude","CAP_FACE",FACE,{"disambiguationData":[OSD([sQuery(id+"F16.wireOp",EDGE,"E44.0"),sQuery(id+"F16.wireOp",EDGE,"E44.1"),sQuery(id+"F16.wireOp",EDGE,"E45"),sQuery(id+"F16.wireOp",EDGE,"E46"),sQuery(id+"F16.wireOp",EDGE,"E47"),sQuery(id+"F16.wireOp",EDGE,"E48")])],"isStart":false})]});
            extrude(context, id + "F19", {"entities" : qUnion([Q0]), "operationType" : NewBodyOperationType.REMOVE, "endBound" : BoundingType.UP_TO_SURFACE, "oppositeDirection" : true, "endBoundEntityFace" : qUnion([Q1]), "depth" : 25.4 * mm});
        }
        {
            var Q0;
            Q0=makeQuery(id+"F17.boolean.opBoolean","MERGE",FACE,{"derivedFrom":[makeQuery(id+"F15.boolean.opBoolean","MERGE",FACE,{"derivedFrom":[makeQuery(id+"F7.boolean.opBoolean","MERGE",FACE,{"derivedFrom":[makeQuery(id+"F5.boolean.opBoolean","MERGE",FACE,{"derivedFrom":[makeQuery(id+"F1.opExtrude","CAP_FACE",FACE,{"disambiguationData":[OSD([sQuery(id+"F0.wireOp",EDGE,"E0"),sQuery(id+"F0.wireOp",EDGE,"E1"),sQuery(id+"F0.wireOp",EDGE,"E2"),sQuery(id+"F0.wireOp",EDGE,"E3"),sQuery(id+"F0.wireOp",EDGE,"E4")])],"isStart":true}),makeQuery(id+"F5.opExtrude","CAP_FACE",FACE,{"disambiguationData":[OSD([sQuery(id+"F4.wireOp",EDGE,"E7"),sQuery(id+"F4.wireOp",EDGE,"E8"),sQuery(id+"F4.wireOp",EDGE,"E9"),sQuery(id+"F4.wireOp",EDGE,"E10")])],"isStart":true})]}),makeQuery(id+"F7.opExtrude","CAP_FACE",FACE,{"disambiguationData":[OSD([sQuery(id+"F6.wireOp",EDGE,"E11"),sQuery(id+"F6.wireOp",EDGE,"E12"),sQuery(id+"F6.wireOp",EDGE,"E13"),sQuery(id+"F6.wireOp",EDGE,"E14")])],"isStart":true})]}),makeQuery(id+"F15.opExtrude","CAP_FACE",FACE,{"disambiguationData":[OSD([sQuery(id+"F10.wireOp",EDGE,"E16"),sQuery(id+"F10.wireOp",EDGE,"E17"),sQuery(id+"F10.wireOp",EDGE,"E18"),sQuery(id+"F10.wireOp",EDGE,"E19")])],"isStart":true}),makeQuery(id+"F15.opExtrude","CAP_FACE",FACE,{"disambiguationData":[OSD([sQuery(id+"F11.wireOp",EDGE,"E20"),sQuery(id+"F11.wireOp",EDGE,"E21"),sQuery(id+"F11.wireOp",EDGE,"E22"),sQuery(id+"F11.wireOp",EDGE,"E23")])],"isStart":true}),makeQuery(id+"F15.opExtrude","CAP_FACE",FACE,{"disambiguationData":[OSD([sQuery(id+"F12.wireOp",EDGE,"E24"),sQuery(id+"F12.wireOp",EDGE,"E25"),sQuery(id+"F12.wireOp",EDGE,"E26"),sQuery(id+"F12.wireOp",EDGE,"E27")])],"isStart":true}),makeQuery(id+"F15.opExtrude","CAP_FACE",FACE,{"disambiguationData":[OSD([sQuery(id+"F13.wireOp",EDGE,"E28"),sQuery(id+"F13.wireOp",EDGE,"E29"),sQuery(id+"F13.wireOp",EDGE,"E30"),sQuery(id+"F13.wireOp",EDGE,"E31"),sQuery(id+"F13.wireOp",EDGE,"E32"),sQuery(id+"F13.wireOp",EDGE,"E33")])],"isStart":true}),makeQuery(id+"F15.opExtrude","CAP_FACE",FACE,{"disambiguationData":[OSD([sQuery(id+"F14.wireOp",EDGE,"E34"),sQuery(id+"F14.wireOp",EDGE,"E35"),sQuery(id+"F14.wireOp",EDGE,"E36"),sQuery(id+"F14.wireOp",EDGE,"E37"),sQuery(id+"F14.wireOp",EDGE,"E38"),sQuery(id+"F14.wireOp",EDGE,"E39")])],"isStart":true}),makeQuery(id+"F15.opExtrude","CAP_FACE",FACE,{"disambiguationData":[OSD([sQuery(id+"F14.wireOp",EDGE,"E40"),sQuery(id+"F14.wireOp",EDGE,"E41"),sQuery(id+"F14.wireOp",EDGE,"E42"),sQuery(id+"F14.wireOp",EDGE,"E43")])],"isStart":true})]}),makeQuery(id+"F17.opExtrude","CAP_FACE",FACE,{"disambiguationData":[OSD([sQuery(id+"F16.wireOp",EDGE,"E44.0"),sQuery(id+"F16.wireOp",EDGE,"E44.1"),sQuery(id+"F16.wireOp",EDGE,"E45"),sQuery(id+"F16.wireOp",EDGE,"E46"),sQuery(id+"F16.wireOp",EDGE,"E47"),sQuery(id+"F16.wireOp",EDGE,"E48")])],"isStart":true})]});
            var sketch = newSketch(context, id + "F20", { "sketchPlane" : qUnion([Q0])});
            skLineSegment(sketch, "E50", {"start": v(2.86, -3.59) * mm, "end": v(21.7, -21.78) * mm});
            skLineSegment(sketch, "E51", {"start": v(21.7, -21.78) * mm, "end": v(22.11, -21.35) * mm});
            skLineSegment(sketch, "E52", {"start": v(22.11, -21.35) * mm, "end": v(3.27, -3.16) * mm});
            skLineSegment(sketch, "E53", {"start": v(3.27, -3.16) * mm, "end": v(2.86, -3.59) * mm});
            skSolve(sketch);
        }
        {
            var Q0;
            Q0 = qSketchRegion(id + "F20", true);
            var Q1;
            Q1=makeQuery(id+"F17.boolean.opBoolean","MERGE",FACE,{"derivedFrom":[makeQuery(id+"F15.boolean.opBoolean","MERGE",FACE,{"derivedFrom":[makeQuery(id+"F7.boolean.opBoolean","MERGE",FACE,{"derivedFrom":[makeQuery(id+"F5.boolean.opBoolean","MERGE",FACE,{"derivedFrom":[makeQuery(id+"F1.opExtrude","CAP_FACE",FACE,{"disambiguationData":[OSD([sQuery(id+"F0.wireOp",EDGE,"E0"),sQuery(id+"F0.wireOp",EDGE,"E1"),sQuery(id+"F0.wireOp",EDGE,"E2"),sQuery(id+"F0.wireOp",EDGE,"E3"),sQuery(id+"F0.wireOp",EDGE,"E4")])],"isStart":false}),makeQuery(id+"F5.opExtrude","CAP_FACE",FACE,{"disambiguationData":[OSD([sQuery(id+"F4.wireOp",EDGE,"E7"),sQuery(id+"F4.wireOp",EDGE,"E8"),sQuery(id+"F4.wireOp",EDGE,"E9"),sQuery(id+"F4.wireOp",EDGE,"E10")])],"isStart":false})]}),makeQuery(id+"F7.opExtrude","CAP_FACE",FACE,{"disambiguationData":[OSD([sQuery(id+"F6.wireOp",EDGE,"E11"),sQuery(id+"F6.wireOp",EDGE,"E12"),sQuery(id+"F6.wireOp",EDGE,"E13"),sQuery(id+"F6.wireOp",EDGE,"E14")])],"isStart":false})]}),makeQuery(id+"F15.opExtrude","CAP_FACE",FACE,{"disambiguationData":[OSD([sQuery(id+"F10.wireOp",EDGE,"E16"),sQuery(id+"F10.wireOp",EDGE,"E17"),sQuery(id+"F10.wireOp",EDGE,"E18"),sQuery(id+"F10.wireOp",EDGE,"E19")])],"isStart":false}),makeQuery(id+"F15.opExtrude","CAP_FACE",FACE,{"disambiguationData":[OSD([sQuery(id+"F11.wireOp",EDGE,"E20"),sQuery(id+"F11.wireOp",EDGE,"E21"),sQuery(id+"F11.wireOp",EDGE,"E22"),sQuery(id+"F11.wireOp",EDGE,"E23")])],"isStart":false}),makeQuery(id+"F15.opExtrude","CAP_FACE",FACE,{"disambiguationData":[OSD([sQuery(id+"F12.wireOp",EDGE,"E24"),sQuery(id+"F12.wireOp",EDGE,"E25"),sQuery(id+"F12.wireOp",EDGE,"E26"),sQuery(id+"F12.wireOp",EDGE,"E27")])],"isStart":false}),makeQuery(id+"F15.opExtrude","CAP_FACE",FACE,{"disambiguationData":[OSD([sQuery(id+"F13.wireOp",EDGE,"E28"),sQuery(id+"F13.wireOp",EDGE,"E29"),sQuery(id+"F13.wireOp",EDGE,"E30"),sQuery(id+"F13.wireOp",EDGE,"E31"),sQuery(id+"F13.wireOp",EDGE,"E32"),sQuery(id+"F13.wireOp",EDGE,"E33")])],"isStart":false}),makeQuery(id+"F15.opExtrude","CAP_FACE",FACE,{"disambiguationData":[OSD([sQuery(id+"F14.wireOp",EDGE,"E34"),sQuery(id+"F14.wireOp",EDGE,"E35"),sQuery(id+"F14.wireOp",EDGE,"E36"),sQuery(id+"F14.wireOp",EDGE,"E37"),sQuery(id+"F14.wireOp",EDGE,"E38"),sQuery(id+"F14.wireOp",EDGE,"E39")])],"isStart":false}),makeQuery(id+"F15.opExtrude","CAP_FACE",FACE,{"disambiguationData":[OSD([sQuery(id+"F14.wireOp",EDGE,"E40"),sQuery(id+"F14.wireOp",EDGE,"E41"),sQuery(id+"F14.wireOp",EDGE,"E42"),sQuery(id+"F14.wireOp",EDGE,"E43")])],"isStart":false})]}),makeQuery(id+"F17.opExtrude","CAP_FACE",FACE,{"disambiguationData":[OSD([sQuery(id+"F16.wireOp",EDGE,"E44.0"),sQuery(id+"F16.wireOp",EDGE,"E44.1"),sQuery(id+"F16.wireOp",EDGE,"E45"),sQuery(id+"F16.wireOp",EDGE,"E46"),sQuery(id+"F16.wireOp",EDGE,"E47"),sQuery(id+"F16.wireOp",EDGE,"E48")])],"isStart":false})]});
            extrude(context, id + "F21", {"entities" : qUnion([Q0]), "operationType" : NewBodyOperationType.REMOVE, "endBound" : BoundingType.UP_TO_SURFACE, "oppositeDirection" : true, "endBoundEntityFace" : qUnion([Q1]), "depth" : 25.4 * mm});
        }
        {
            var Q0;
            Q0=makeQuery(id+"F17.boolean.opBoolean","MERGE",FACE,{"derivedFrom":[makeQuery(id+"F15.boolean.opBoolean","MERGE",FACE,{"derivedFrom":[makeQuery(id+"F7.boolean.opBoolean","MERGE",FACE,{"derivedFrom":[makeQuery(id+"F5.boolean.opBoolean","MERGE",FACE,{"derivedFrom":[makeQuery(id+"F1.opExtrude","CAP_FACE",FACE,{"disambiguationData":[OSD([sQuery(id+"F0.wireOp",EDGE,"E0"),sQuery(id+"F0.wireOp",EDGE,"E1"),sQuery(id+"F0.wireOp",EDGE,"E2"),sQuery(id+"F0.wireOp",EDGE,"E3"),sQuery(id+"F0.wireOp",EDGE,"E4")])],"isStart":true}),makeQuery(id+"F5.opExtrude","CAP_FACE",FACE,{"disambiguationData":[OSD([sQuery(id+"F4.wireOp",EDGE,"E7"),sQuery(id+"F4.wireOp",EDGE,"E8"),sQuery(id+"F4.wireOp",EDGE,"E9"),sQuery(id+"F4.wireOp",EDGE,"E10")])],"isStart":true})]}),makeQuery(id+"F7.opExtrude","CAP_FACE",FACE,{"disambiguationData":[OSD([sQuery(id+"F6.wireOp",EDGE,"E11"),sQuery(id+"F6.wireOp",EDGE,"E12"),sQuery(id+"F6.wireOp",EDGE,"E13"),sQuery(id+"F6.wireOp",EDGE,"E14")])],"isStart":true})]}),makeQuery(id+"F15.opExtrude","CAP_FACE",FACE,{"disambiguationData":[OSD([sQuery(id+"F10.wireOp",EDGE,"E16"),sQuery(id+"F10.wireOp",EDGE,"E17"),sQuery(id+"F10.wireOp",EDGE,"E18"),sQuery(id+"F10.wireOp",EDGE,"E19")])],"isStart":true}),makeQuery(id+"F15.opExtrude","CAP_FACE",FACE,{"disambiguationData":[OSD([sQuery(id+"F11.wireOp",EDGE,"E20"),sQuery(id+"F11.wireOp",EDGE,"E21"),sQuery(id+"F11.wireOp",EDGE,"E22"),sQuery(id+"F11.wireOp",EDGE,"E23")])],"isStart":true}),makeQuery(id+"F15.opExtrude","CAP_FACE",FACE,{"disambiguationData":[OSD([sQuery(id+"F12.wireOp",EDGE,"E24"),sQuery(id+"F12.wireOp",EDGE,"E25"),sQuery(id+"F12.wireOp",EDGE,"E26"),sQuery(id+"F12.wireOp",EDGE,"E27")])],"isStart":true}),makeQuery(id+"F15.opExtrude","CAP_FACE",FACE,{"disambiguationData":[OSD([sQuery(id+"F13.wireOp",EDGE,"E28"),sQuery(id+"F13.wireOp",EDGE,"E29"),sQuery(id+"F13.wireOp",EDGE,"E30"),sQuery(id+"F13.wireOp",EDGE,"E31"),sQuery(id+"F13.wireOp",EDGE,"E32"),sQuery(id+"F13.wireOp",EDGE,"E33")])],"isStart":true}),makeQuery(id+"F15.opExtrude","CAP_FACE",FACE,{"disambiguationData":[OSD([sQuery(id+"F14.wireOp",EDGE,"E34"),sQuery(id+"F14.wireOp",EDGE,"E35"),sQuery(id+"F14.wireOp",EDGE,"E36"),sQuery(id+"F14.wireOp",EDGE,"E37"),sQuery(id+"F14.wireOp",EDGE,"E38"),sQuery(id+"F14.wireOp",EDGE,"E39")])],"isStart":true}),makeQuery(id+"F15.opExtrude","CAP_FACE",FACE,{"disambiguationData":[OSD([sQuery(id+"F14.wireOp",EDGE,"E40"),sQuery(id+"F14.wireOp",EDGE,"E41"),sQuery(id+"F14.wireOp",EDGE,"E42"),sQuery(id+"F14.wireOp",EDGE,"E43")])],"isStart":true})]}),makeQuery(id+"F17.opExtrude","CAP_FACE",FACE,{"disambiguationData":[OSD([sQuery(id+"F16.wireOp",EDGE,"E44.0"),sQuery(id+"F16.wireOp",EDGE,"E44.1"),sQuery(id+"F16.wireOp",EDGE,"E45"),sQuery(id+"F16.wireOp",EDGE,"E46"),sQuery(id+"F16.wireOp",EDGE,"E47"),sQuery(id+"F16.wireOp",EDGE,"E48")])],"isStart":true})]});
            var sketch = newSketch(context, id + "F22", { "sketchPlane" : qUnion([Q0])});
            skArc(sketch, "E54", {"start": v(24.08, -21.14) * mm, "mid": v(24.27, -22.5) * mm, "end": v(25.64, -22.64) * mm});
            skLineSegment(sketch, "E55", {"start": v(24.08, -21.14) * mm, "end": v(25.64, -22.64) * mm});
            skSolve(sketch);
        }
        {
            var Q0;
            Q0 = qSketchRegion(id + "F22", true);
            var Q1;
            Q1=makeQuery(id+"F17.boolean.opBoolean","MERGE",FACE,{"derivedFrom":[makeQuery(id+"F15.boolean.opBoolean","MERGE",FACE,{"derivedFrom":[makeQuery(id+"F7.boolean.opBoolean","MERGE",FACE,{"derivedFrom":[makeQuery(id+"F5.boolean.opBoolean","MERGE",FACE,{"derivedFrom":[makeQuery(id+"F1.opExtrude","CAP_FACE",FACE,{"disambiguationData":[OSD([sQuery(id+"F0.wireOp",EDGE,"E0"),sQuery(id+"F0.wireOp",EDGE,"E1"),sQuery(id+"F0.wireOp",EDGE,"E2"),sQuery(id+"F0.wireOp",EDGE,"E3"),sQuery(id+"F0.wireOp",EDGE,"E4")])],"isStart":false}),makeQuery(id+"F5.opExtrude","CAP_FACE",FACE,{"disambiguationData":[OSD([sQuery(id+"F4.wireOp",EDGE,"E7"),sQuery(id+"F4.wireOp",EDGE,"E8"),sQuery(id+"F4.wireOp",EDGE,"E9"),sQuery(id+"F4.wireOp",EDGE,"E10")])],"isStart":false})]}),makeQuery(id+"F7.opExtrude","CAP_FACE",FACE,{"disambiguationData":[OSD([sQuery(id+"F6.wireOp",EDGE,"E11"),sQuery(id+"F6.wireOp",EDGE,"E12"),sQuery(id+"F6.wireOp",EDGE,"E13"),sQuery(id+"F6.wireOp",EDGE,"E14")])],"isStart":false})]}),makeQuery(id+"F15.opExtrude","CAP_FACE",FACE,{"disambiguationData":[OSD([sQuery(id+"F10.wireOp",EDGE,"E16"),sQuery(id+"F10.wireOp",EDGE,"E17"),sQuery(id+"F10.wireOp",EDGE,"E18"),sQuery(id+"F10.wireOp",EDGE,"E19")])],"isStart":false}),makeQuery(id+"F15.opExtrude","CAP_FACE",FACE,{"disambiguationData":[OSD([sQuery(id+"F11.wireOp",EDGE,"E20"),sQuery(id+"F11.wireOp",EDGE,"E21"),sQuery(id+"F11.wireOp",EDGE,"E22"),sQuery(id+"F11.wireOp",EDGE,"E23")])],"isStart":false}),makeQuery(id+"F15.opExtrude","CAP_FACE",FACE,{"disambiguationData":[OSD([sQuery(id+"F12.wireOp",EDGE,"E24"),sQuery(id+"F12.wireOp",EDGE,"E25"),sQuery(id+"F12.wireOp",EDGE,"E26"),sQuery(id+"F12.wireOp",EDGE,"E27")])],"isStart":false}),makeQuery(id+"F15.opExtrude","CAP_FACE",FACE,{"disambiguationData":[OSD([sQuery(id+"F13.wireOp",EDGE,"E28"),sQuery(id+"F13.wireOp",EDGE,"E29"),sQuery(id+"F13.wireOp",EDGE,"E30"),sQuery(id+"F13.wireOp",EDGE,"E31"),sQuery(id+"F13.wireOp",EDGE,"E32"),sQuery(id+"F13.wireOp",EDGE,"E33")])],"isStart":false}),makeQuery(id+"F15.opExtrude","CAP_FACE",FACE,{"disambiguationData":[OSD([sQuery(id+"F14.wireOp",EDGE,"E34"),sQuery(id+"F14.wireOp",EDGE,"E35"),sQuery(id+"F14.wireOp",EDGE,"E36"),sQuery(id+"F14.wireOp",EDGE,"E37"),sQuery(id+"F14.wireOp",EDGE,"E38"),sQuery(id+"F14.wireOp",EDGE,"E39")])],"isStart":false}),makeQuery(id+"F15.opExtrude","CAP_FACE",FACE,{"disambiguationData":[OSD([sQuery(id+"F14.wireOp",EDGE,"E40"),sQuery(id+"F14.wireOp",EDGE,"E41"),sQuery(id+"F14.wireOp",EDGE,"E42"),sQuery(id+"F14.wireOp",EDGE,"E43")])],"isStart":false})]}),makeQuery(id+"F17.opExtrude","CAP_FACE",FACE,{"disambiguationData":[OSD([sQuery(id+"F16.wireOp",EDGE,"E44.0"),sQuery(id+"F16.wireOp",EDGE,"E44.1"),sQuery(id+"F16.wireOp",EDGE,"E45"),sQuery(id+"F16.wireOp",EDGE,"E46"),sQuery(id+"F16.wireOp",EDGE,"E47"),sQuery(id+"F16.wireOp",EDGE,"E48")])],"isStart":false})]});
            extrude(context, id + "F23", {"entities" : qUnion([Q0]), "operationType" : NewBodyOperationType.REMOVE, "endBound" : BoundingType.UP_TO_SURFACE, "oppositeDirection" : true, "endBoundEntityFace" : qUnion([Q1]), "depth" : 25.4 * mm});
        }
        {
            var Q0;
            Q0=makeQuery(id+"F1.opExtrude","SWEPT_EDGE",EDGE,{"disambiguationData":[OSD([sQuery(id+"F0.wireOp",EDGE,"E3"),sQuery(id+"F0.wireOp",EDGE,"E4")])]});
            var Q1;
            Q1=makeQuery(id+"F17.opExtrude","SWEPT_EDGE",EDGE,{"disambiguationData":[OSD([sQuery(id+"F16.wireOp",EDGE,"E44.0"),sQuery(id+"F16.wireOp",EDGE,"E45")])]});
            var Q2;
            Q2=makeQuery(id+"F17.opExtrude","SWEPT_EDGE",EDGE,{"disambiguationData":[OSD([sQuery(id+"F16.wireOp",EDGE,"E44.1"),sQuery(id+"F16.wireOp",EDGE,"E46")])]});
            fillet(context, id + "F24", {"entities" : qUnion([Q0, Q1, Q2]), "radius" : 0.5 * mm, "allowEdgeOverflow" : false});
        }
        {
            var Q0;
            Q0=makeQuery(id+"F2.opShell","OFFSET_EDGE",EDGE,{"disambiguationData":[OSD([sQuery(id+"F0.wireOp",EDGE,"E0"),sQuery(id+"F0.wireOp",EDGE,"E1")])]});
            var Q1;
            Q1=makeQuery(id+"F17.opExtrude","SWEPT_EDGE",EDGE,{"disambiguationData":[OSD([sQuery(id+"F16.wireOp",EDGE,"E44.0"),sQuery(id+"F16.wireOp",EDGE,"E44.1")])]});
            fillet(context, id + "F25", {"entities" : qUnion([Q0, Q1]), "radius" : 6.35 * mm, "tangentPropagation" : true, "allowEdgeOverflow" : false});
        }
        {
            var Q0;
            Q0=makeQuery(id+"F7.opExtrude","SWEPT_EDGE",EDGE,{"disambiguationData":[OSD([sQuery(id+"F6.wireOp",EDGE,"E13"),sQuery(id+"F6.wireOp",EDGE,"E14")])]});
            var Q1;
            Q1=makeQuery(id+"F9.boolean.opBoolean","INTERSECT",EDGE,{"derivedFrom":[makeQuery(id+"F5.opExtrude","SWEPT_FACE",FACE,{"disambiguationData":[OSD([sQuery(id+"F4.wireOp",EDGE,"E8")])]}),makeQuery(id+"F9.opExtrude","SWEPT_FACE",FACE,{"disambiguationData":[OSD([sQuery(id+"F8.wireOp",EDGE,"E15")])]})]});
            fillet(context, id + "F26", {"entities" : qUnion([Q0, Q1]), "radius" : 0.25 * mm, "tangentPropagation" : true, "allowEdgeOverflow" : false});
        }
    });
